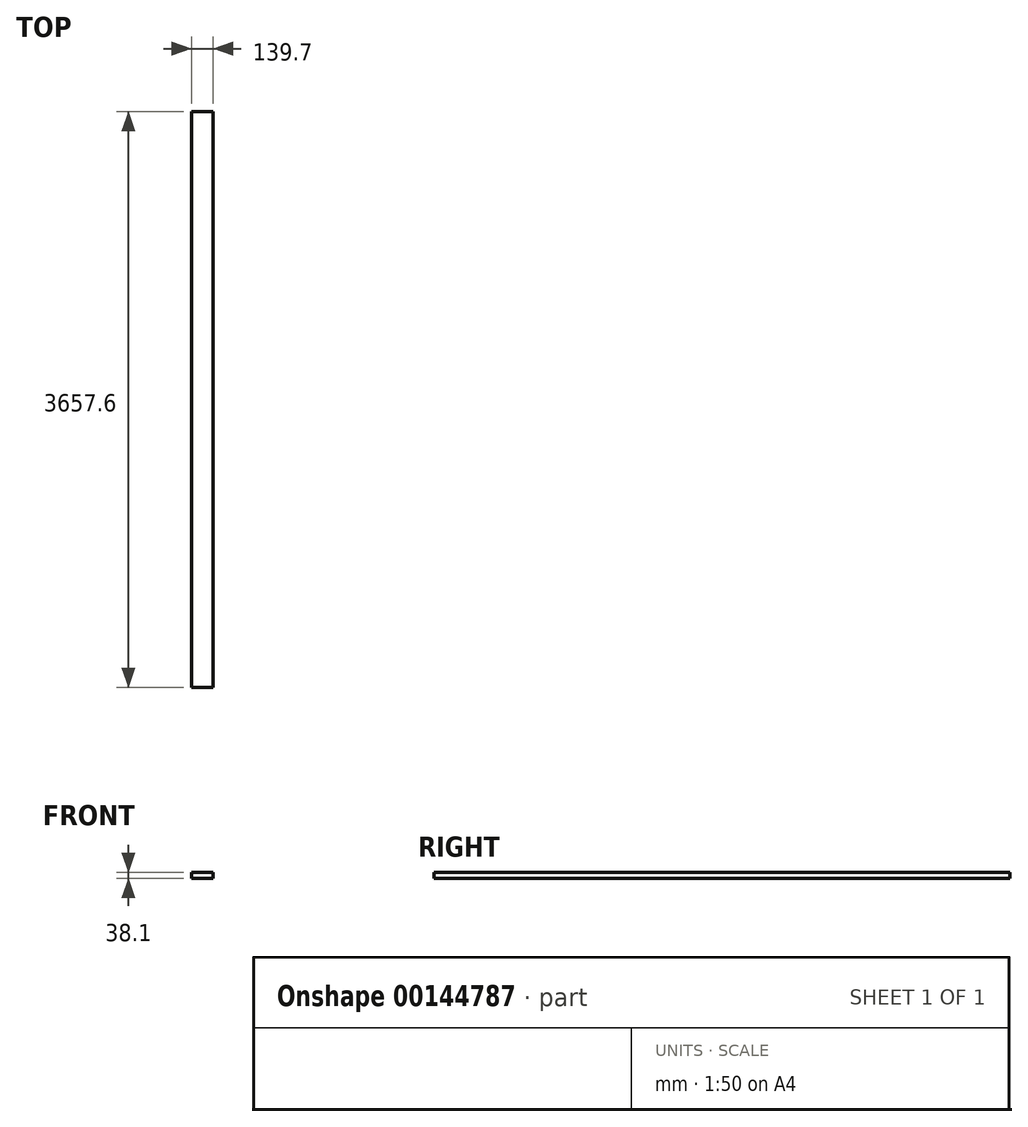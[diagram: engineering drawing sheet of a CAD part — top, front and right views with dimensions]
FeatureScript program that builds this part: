
annotation { "Feature Type Name" : "Feature", "Feature Type Description" : "" }
export const myFeature = defineFeature(function(context is Context, id is Id, definition is map)
    precondition{}
    {
        {
            var Q0;
            Q0=qCreatedBy(makeId("Front.planeOp"),FACE);
            var sketch = newSketch(context, id + "F0", { "sketchPlane" : qUnion([Q0])});
            skLineSegment(sketch, "E0.bottom", {"start": v(0, 0) * mm, "end": v(139.7, 0) * mm});
            skLineSegment(sketch, "E0.top", {"start": v(0, 38.1) * mm, "end": v(139.7, 38.1) * mm});
            skLineSegment(sketch, "E0.left", {"start": v(0, 0) * mm, "end": v(0, 38.1) * mm});
            skLineSegment(sketch, "E0.right", {"start": v(139.7, 0) * mm, "end": v(139.7, 38.1) * mm});
            skSolve(sketch);
        }
        {
            var Q0;
            Q0=makeQuery(id+"F0.imprint","IMPRINT",FACE,{"disambiguationData":[TD([[makeQuery(id+"F0.imprint","IMPRINT",EDGE,{"derivedFrom":sQuery(id+"F0.wireOp",EDGE,"E0.bottom")}),1.0]])]});
            extrude(context, id + "F1", {"entities" : qUnion([Q0]), "depth" : 3657.6 * mm});
        }
    });
